# Revit family: Curved Walls Radius
name_source: partatom
category: Generic Models
revit_build: Autodesk Revit 2016 (Build: 20150714_1515(x64)
units: mm (PartAtom-declared; Revit-internal decimal feet)

## family parameters
Always vertical = No
Can host rebar = No
Cut with Voids When Loaded = No
Part Type = Normal
Room Calculation Point = No
Round Connector Dimension = Use Diameter
Shared = No
Work Plane-Based = Yes

## types (3) — shared parameters
Default Elevation = 0' - 0"
Description = Prefabricated Drywall Profiles
Manufacturer = Curved Walls Inc
URL = www.curvedwalls.ca

## per-type parameters (varying)
| type | Cove Radius (6" & 12" Standard) | GWB Thickness (1/2") | Overall Dimension A | Overall Dimension B | Straight Transition Length A | Straight Transition Length B |
| 1/4" Thk. x 6" R x 8" W x 8" H | 0' - 6" | 0' - 0 1/4" | 0' - 8" | 0' - 8" | 0' - 2" | 0' - 2" |
| 1/2" Thk. x 12" R x 18" W x 20" H | 1' - 0" | 0' - 0 1/2" | 1' - 6" | 1' - 8" | 0' - 6" | 0' - 8" |
| 1/2" Thk. x Custom R x 14" W x 14" H | 0' - 10" | 0' - 0 1/2" | 1' - 2" | 1' - 2" | 0' - 4" | 0' - 4" |

## geometry (parser evidence)
native form markers: Blend x4, Sweep x2
no freeform markers — native parametric forms only
